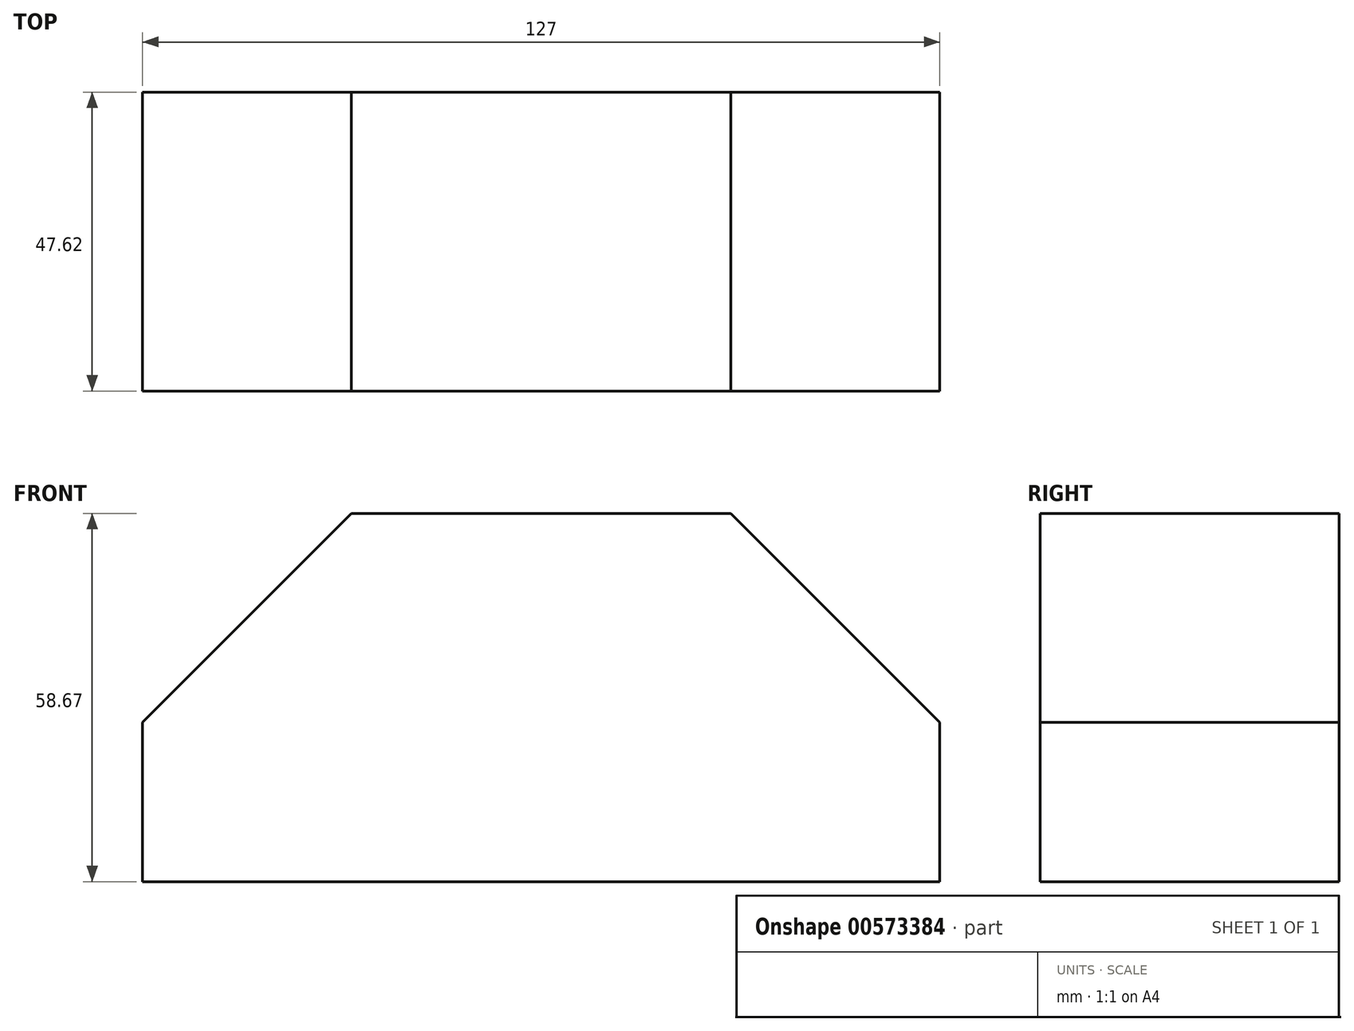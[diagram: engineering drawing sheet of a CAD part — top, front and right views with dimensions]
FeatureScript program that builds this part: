
annotation { "Feature Type Name" : "Feature", "Feature Type Description" : "" }
export const myFeature = defineFeature(function(context is Context, id is Id, definition is map)
    precondition{}
    {
        {
            var Q0;
            Q0=qCreatedBy(makeId("Front.planeOp"),FACE);
            var sketch = newSketch(context, id + "F0", { "sketchPlane" : qUnion([Q0])});
            skLineSegment(sketch, "E0", {"start": v(-64.32, -61.74) * mm, "end": v(62.68, -61.74) * mm});
            skLineSegment(sketch, "E1", {"start": v(-31.05, -3.07) * mm, "end": v(29.4, -3.07) * mm});
            skLineSegment(sketch, "E2", {"start": v(62.68, -36.34) * mm, "end": v(62.68, -61.74) * mm});
            skLineSegment(sketch, "E3", {"start": v(-64.32, -36.34) * mm, "end": v(-31.05, -3.07) * mm});
            skLineSegment(sketch, "E4", {"start": v(29.4, -3.07) * mm, "end": v(62.68, -36.34) * mm});
            skLineSegment(sketch, "E5", {"start": v(-64.32, -36.34) * mm, "end": v(-64.32, -61.74) * mm});
            skSolve(sketch);
        }
        {
            var Q0;
            Q0=makeQuery(id+"F0.imprint","IMPRINT",FACE,{"disambiguationData":[TD([[makeQuery(id+"F0.imprint","IMPRINT",EDGE,{"derivedFrom":sQuery(id+"F0.wireOp",EDGE,"E0")}),1.0]])]});
            extrude(context, id + "F1", {"entities" : qUnion([Q0]), "depth" : 47.62 * mm, "offsetDistance" : 25.4 * mm});
        }
    });
